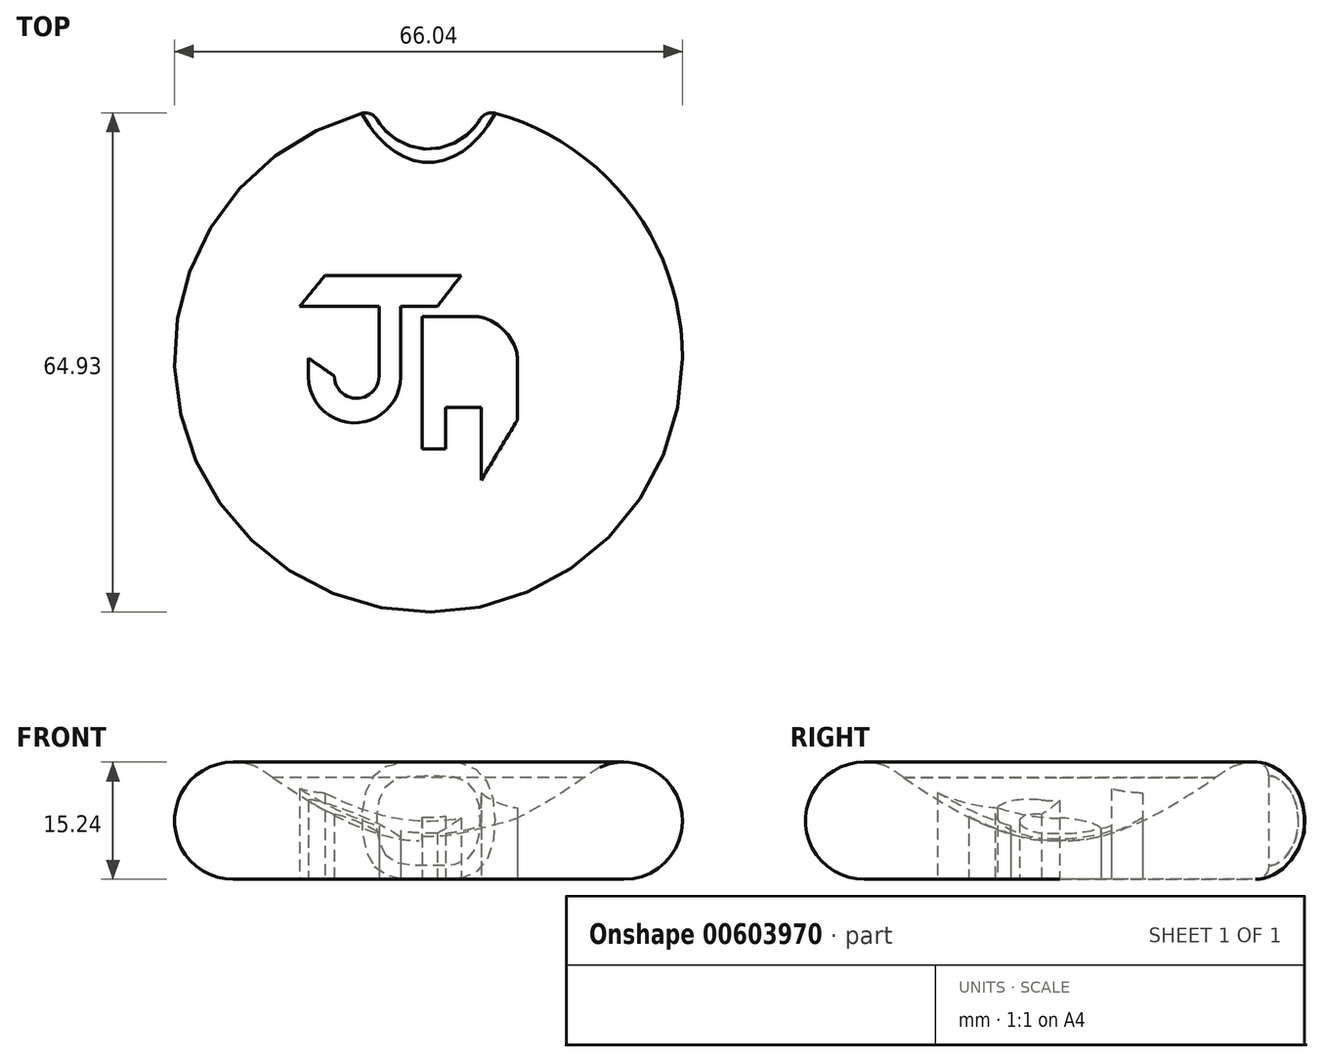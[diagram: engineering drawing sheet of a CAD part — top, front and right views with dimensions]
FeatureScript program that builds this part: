
annotation { "Feature Type Name" : "Feature", "Feature Type Description" : "" }
export const myFeature = defineFeature(function(context is Context, id is Id, definition is map)
    precondition{}
    {
        {
            var Q0;
            Q0=qCreatedBy(makeId("Front.planeOp"),FACE);
            var sketch = newSketch(context, id + "F0", { "sketchPlane" : qUnion([Q0])});
            skCircle(sketch, "E0", {"center": v(-25.4, 7.62) * mm, "radius": 7.62 * mm});
            skLineSegment(sketch, "E1", {"start": v(0, 5.08) * mm, "end": v(0, 0) * mm});
            skLineSegment(sketch, "E2", {"start": v(0, 0) * mm, "end": v(-25.4, 0) * mm});
            skFitSpline(sketch, "E3", {"points": [v(-22.3, 14.58) * mm, v(0, 5.08) * mm], "startDerivative": vector(4.62, -2.05) * mm, "endDerivative": vector(26.98, 2.67) * mm});
            skSolve(sketch);
        }
        {
            var Q0;
            {var subQ0=sQuery(id+"F0.wireOp",EDGE,"E0");var subQ1=makeQuery(id+"F0.imprint","INTERSECT",VERTEX,{"derivedFrom":[subQ0,sQuery(id+"F0.wireOp",EDGE,"E2")]});Q0=makeQuery(id+"F0.imprint","IMPRINT",FACE,{"disambiguationData":[TD([[makeQuery(id+"F0.imprint","IMPRINT",EDGE,{"disambiguationData":[TD([[subQ1,1.0]])],"derivedFrom":subQ0}),1.0]])]});}
            var Q1;
            Q1=makeQuery(id+"F0.imprint","IMPRINT",FACE,{"disambiguationData":[TD([[makeQuery(id+"F0.imprint","IMPRINT",EDGE,{"derivedFrom":sQuery(id+"F0.wireOp",EDGE,"E1")}),-1.0]])]});
            var Q2;
            Q2=sQuery(id+"F0.wireOp",EDGE,"E1");
            revolve(context, id + "F1", {"entities" : qUnion([Q0, Q1]), "axis" : qUnion([Q2]), "revolveType" : RevolveType.FULL});
        }
        {
            var Q0;
            Q0=qCreatedBy(makeId("Top.planeOp"),FACE);
            var sketch = newSketch(context, id + "F2", { "sketchPlane" : qUnion([Q0])});
            skLineSegment(sketch, "E4", {"start": v(0, 0) * mm, "end": v(0, 34.94) * mm});
            skCircle(sketch, "E5", {"center": v(0, 34.94) * mm, "radius": 7.74 * mm});
            skSolve(sketch);
        }
        {
            var Q0;
            Q0=makeQuery(id+"FB6AYjDz6TvVvHu_1.7.F2.imprint","IMPRINT",FACE,{"disambiguationData":[TD([[makeQuery(id+"FB6AYjDz6TvVvHu_1.7.F2.imprint","IMPRINT",EDGE,{"derivedFrom":sQuery(id+"FB6AYjDz6TvVvHu_1.7.F2.wireOp",EDGE,"E5")}),1.0]])]});
            var Q1;
            Q1=makeQuery(id+"F2.imprint","IMPRINT",FACE,{"disambiguationData":[TD([[makeQuery(id+"F2.imprint","IMPRINT",EDGE,{"derivedFrom":sQuery(id+"F2.wireOp",EDGE,"E5")}),1.0]])]});
            var Q2;
            Q2=makeQuery(id+"FB6AYjDz6TvVvHu_1.1.F2.imprint","IMPRINT",FACE,{"disambiguationData":[TD([[makeQuery(id+"FB6AYjDz6TvVvHu_1.1.F2.imprint","IMPRINT",EDGE,{"derivedFrom":sQuery(id+"FB6AYjDz6TvVvHu_1.1.F2.wireOp",EDGE,"E5")}),1.0]])]});
            var Q3;
            Q3=makeQuery(id+"FB6AYjDz6TvVvHu_1.2.F2.imprint","IMPRINT",FACE,{"disambiguationData":[TD([[makeQuery(id+"FB6AYjDz6TvVvHu_1.2.F2.imprint","IMPRINT",EDGE,{"derivedFrom":sQuery(id+"FB6AYjDz6TvVvHu_1.2.F2.wireOp",EDGE,"E5")}),1.0]])]});
            var Q4;
            Q4=makeQuery(id+"FB6AYjDz6TvVvHu_1.3.F2.imprint","IMPRINT",FACE,{"disambiguationData":[TD([[makeQuery(id+"FB6AYjDz6TvVvHu_1.3.F2.imprint","IMPRINT",EDGE,{"derivedFrom":sQuery(id+"FB6AYjDz6TvVvHu_1.3.F2.wireOp",EDGE,"E5")}),1.0]])]});
            var Q5;
            Q5=makeQuery(id+"FB6AYjDz6TvVvHu_1.4.F2.imprint","IMPRINT",FACE,{"disambiguationData":[TD([[makeQuery(id+"FB6AYjDz6TvVvHu_1.4.F2.imprint","IMPRINT",EDGE,{"derivedFrom":sQuery(id+"FB6AYjDz6TvVvHu_1.4.F2.wireOp",EDGE,"E5")}),1.0]])]});
            var Q6;
            Q6=makeQuery(id+"FB6AYjDz6TvVvHu_1.5.F2.imprint","IMPRINT",FACE,{"disambiguationData":[TD([[makeQuery(id+"FB6AYjDz6TvVvHu_1.5.F2.imprint","IMPRINT",EDGE,{"derivedFrom":sQuery(id+"FB6AYjDz6TvVvHu_1.5.F2.wireOp",EDGE,"E5")}),1.0]])]});
            var Q7;
            Q7=makeQuery(id+"FB6AYjDz6TvVvHu_1.6.F2.imprint","IMPRINT",FACE,{"disambiguationData":[TD([[makeQuery(id+"FB6AYjDz6TvVvHu_1.6.F2.imprint","IMPRINT",EDGE,{"derivedFrom":sQuery(id+"FB6AYjDz6TvVvHu_1.6.F2.wireOp",EDGE,"E5")}),1.0]])]});
            var Q8;
            Q8=makeQuery(id+"FB6AYjDz6TvVvHu_1.8.F2.imprint","IMPRINT",FACE,{"disambiguationData":[TD([[makeQuery(id+"FB6AYjDz6TvVvHu_1.8.F2.imprint","IMPRINT",EDGE,{"derivedFrom":sQuery(id+"FB6AYjDz6TvVvHu_1.8.F2.wireOp",EDGE,"E5")}),1.0]])]});
            extrude(context, id + "F3", {"entities" : qUnion([Q0, Q1, Q2, Q3, Q4, Q5, Q6, Q7, Q8]), "operationType" : NewBodyOperationType.REMOVE, "depth" : 18.54 * mm, "offsetDistance" : 25.4 * mm});
        }
        {
            var Q0;
            Q0=makeQuery(id+"F3.boolean.opBoolean","INTERSECT",EDGE,{"derivedFrom":[makeQuery(id+"F1.opRevolve","SWEPT_FACE",FACE,{"disambiguationData":[OSD([sQuery(id+"F0.wireOp",EDGE,"E0")])]}),makeQuery(id+"F3.opExtrude","SWEPT_FACE",FACE,{"disambiguationData":[OSD([sQuery(id+"FB6AYjDz6TvVvHu_1.8.F2.wireOp",EDGE,"E5")])]})]});
            var Q1;
            Q1=makeQuery(id+"F3.boolean.opBoolean","INTERSECT",EDGE,{"derivedFrom":[makeQuery(id+"F1.opRevolve","SWEPT_FACE",FACE,{"disambiguationData":[OSD([sQuery(id+"F0.wireOp",EDGE,"E0")])]}),makeQuery(id+"F3.opExtrude","SWEPT_FACE",FACE,{"disambiguationData":[OSD([sQuery(id+"F2.wireOp",EDGE,"E5")])]})]});
            var Q2;
            Q2=makeQuery(id+"F3.boolean.opBoolean","COPY",FACE,{"derivedFrom":makeQuery(id+"F3.opExtrude","SWEPT_FACE",FACE,{"disambiguationData":[OSD([sQuery(id+"FB6AYjDz6TvVvHu_1.1.F2.wireOp",EDGE,"E5")])]})});
            var Q3;
            Q3=makeQuery(id+"F3.boolean.opBoolean","INTERSECT",EDGE,{"derivedFrom":[makeQuery(id+"F1.opRevolve","SWEPT_FACE",FACE,{"disambiguationData":[OSD([sQuery(id+"F0.wireOp",EDGE,"E0")])]}),makeQuery(id+"F3.opExtrude","SWEPT_FACE",FACE,{"disambiguationData":[OSD([sQuery(id+"FB6AYjDz6TvVvHu_1.2.F2.wireOp",EDGE,"E5")])]})]});
            var Q4;
            Q4=makeQuery(id+"F3.boolean.opBoolean","INTERSECT",EDGE,{"derivedFrom":[makeQuery(id+"F1.opRevolve","SWEPT_FACE",FACE,{"disambiguationData":[OSD([sQuery(id+"F0.wireOp",EDGE,"E0")])]}),makeQuery(id+"F3.opExtrude","SWEPT_FACE",FACE,{"disambiguationData":[OSD([sQuery(id+"FB6AYjDz6TvVvHu_1.3.F2.wireOp",EDGE,"E5")])]})]});
            var Q5;
            Q5=makeQuery(id+"F3.boolean.opBoolean","INTERSECT",EDGE,{"derivedFrom":[makeQuery(id+"F1.opRevolve","SWEPT_FACE",FACE,{"disambiguationData":[OSD([sQuery(id+"F0.wireOp",EDGE,"E0")])]}),makeQuery(id+"F3.opExtrude","SWEPT_FACE",FACE,{"disambiguationData":[OSD([sQuery(id+"FB6AYjDz6TvVvHu_1.4.F2.wireOp",EDGE,"E5")])]})]});
            var Q6;
            Q6=makeQuery(id+"F3.boolean.opBoolean","INTERSECT",EDGE,{"derivedFrom":[makeQuery(id+"F1.opRevolve","SWEPT_FACE",FACE,{"disambiguationData":[OSD([sQuery(id+"F0.wireOp",EDGE,"E0")])]}),makeQuery(id+"F3.opExtrude","SWEPT_FACE",FACE,{"disambiguationData":[OSD([sQuery(id+"FB6AYjDz6TvVvHu_1.5.F2.wireOp",EDGE,"E5")])]})]});
            var Q7;
            Q7=makeQuery(id+"F3.boolean.opBoolean","INTERSECT",EDGE,{"derivedFrom":[makeQuery(id+"F1.opRevolve","SWEPT_FACE",FACE,{"disambiguationData":[OSD([sQuery(id+"F0.wireOp",EDGE,"E0")])]}),makeQuery(id+"F3.opExtrude","SWEPT_FACE",FACE,{"disambiguationData":[OSD([sQuery(id+"FB6AYjDz6TvVvHu_1.6.F2.wireOp",EDGE,"E5")])]})]});
            var Q8;
            Q8=makeQuery(id+"F3.boolean.opBoolean","INTERSECT",EDGE,{"derivedFrom":[makeQuery(id+"F1.opRevolve","SWEPT_FACE",FACE,{"disambiguationData":[OSD([sQuery(id+"F0.wireOp",EDGE,"E0")])]}),makeQuery(id+"F3.opExtrude","SWEPT_FACE",FACE,{"disambiguationData":[OSD([sQuery(id+"FB6AYjDz6TvVvHu_1.7.F2.wireOp",EDGE,"E5")])]})]});
            fillet(context, id + "F4", {"entities" : qUnion([Q0, Q1, Q2, Q3, Q4, Q5, Q6, Q7, Q8]), "radius" : 1.78 * mm, "tangentPropagation" : true, "allowEdgeOverflow" : false});
        }
        {
            var Q0;
            Q0=qCreatedBy(makeId("Top.planeOp"),FACE);
            var sketch = newSketch(context, id + "F5", { "sketchPlane" : qUnion([Q0])});
            skLineSegment(sketch, "E6", {"start": v(-13.44, 10.77) * mm, "end": v(-16.76, 6.72) * mm});
            skLineSegment(sketch, "E7", {"start": v(-16.76, 6.72) * mm, "end": v(-6.44, 6.72) * mm});
            skLineSegment(sketch, "E8", {"start": v(-6.44, 6.72) * mm, "end": v(-6.44, -2.32) * mm});
            skLineSegment(sketch, "E9", {"start": v(-13.44, 10.77) * mm, "end": v(4.26, 10.77) * mm});
            skLineSegment(sketch, "E10", {"start": v(4.26, 10.77) * mm, "end": v(1.12, 6.72) * mm});
            skLineSegment(sketch, "E11", {"start": v(1.12, 6.72) * mm, "end": v(-3.62, 6.72) * mm});
            skLineSegment(sketch, "E12", {"start": v(-3.62, 6.72) * mm, "end": v(-3.62, -2.4) * mm});
            skArc(sketch, "E13", {"start": v(-15.61, -2.4) * mm, "mid": v(-9.62, -8.4) * mm, "end": v(-3.62, -2.4) * mm});
            skArc(sketch, "E14", {"start": v(-12.24, -2.32) * mm, "mid": v(-9.34, -5.22) * mm, "end": v(-6.44, -2.32) * mm});
            skLineSegment(sketch, "E15", {"start": v(-15.61, -2.4) * mm, "end": v(-15.61, 0) * mm});
            skLineSegment(sketch, "E16", {"start": v(-15.61, 0) * mm, "end": v(-12.24, -2.32) * mm});
            skLineSegment(sketch, "E17", {"start": v(-0.81, 5.43) * mm, "end": v(-0.81, -11.81) * mm});
            skLineSegment(sketch, "E18", {"start": v(-0.81, -11.81) * mm, "end": v(2.23, -11.81) * mm});
            skLineSegment(sketch, "E19", {"start": v(2.23, -11.81) * mm, "end": v(2.23, -6.37) * mm});
            skLineSegment(sketch, "E20", {"start": v(2.23, -6.37) * mm, "end": v(6.84, -6.37) * mm});
            skLineSegment(sketch, "E21", {"start": v(6.84, -6.37) * mm, "end": v(6.84, -15.86) * mm});
            skLineSegment(sketch, "E22", {"start": v(6.84, -15.86) * mm, "end": v(11.54, -8.07) * mm});
            skLineSegment(sketch, "E23", {"start": v(11.54, -8.07) * mm, "end": v(11.54, 0) * mm});
            skLineSegment(sketch, "E24", {"start": v(-0.81, 5.43) * mm, "end": v(6, 5.43) * mm});
            skFitSpline(sketch, "E25", {"points": [v(6, 5.43) * mm, v(11.54, 0) * mm], "startDerivative": vector(7.75, 0) * mm, "endDerivative": vector(0, -7.75) * mm});
            skSolve(sketch);
        }
        {
            var Q0;
            Q0 = qSketchRegion(id + "F5", true);
            extrude(context, id + "F6", {"entities" : qUnion([Q0]), "operationType" : NewBodyOperationType.REMOVE, "depth" : 23.27 * mm, "offsetDistance" : 25.4 * mm});
        }
    });
